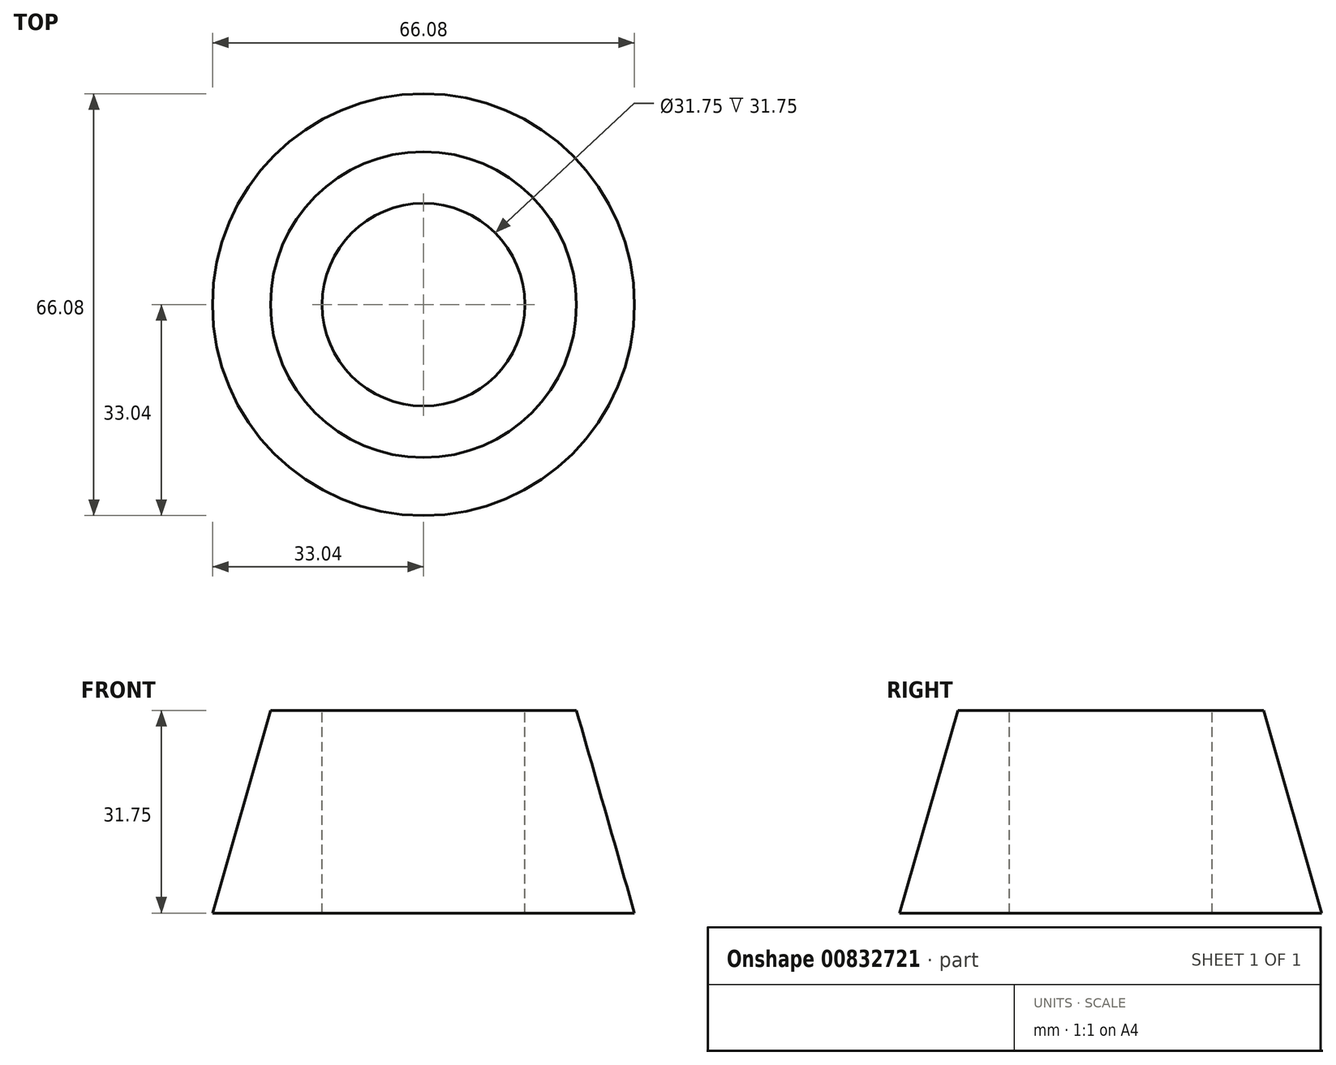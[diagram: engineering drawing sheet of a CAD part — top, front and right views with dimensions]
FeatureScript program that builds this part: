
annotation { "Feature Type Name" : "Feature", "Feature Type Description" : "" }
export const myFeature = defineFeature(function(context is Context, id is Id, definition is map)
    precondition{}
    {
        {
            var Q0;
            Q0=qCreatedBy(makeId("Top.planeOp"),FACE);
            var sketch = newSketch(context, id + "F0", { "sketchPlane" : qUnion([Q0])});
            skCircle(sketch, "E0", {"center": v(0, 0) * mm, "radius": 33.04 * mm});
            skSolve(sketch);
        }
        {
            var Q0;
            Q0=qCreatedBy(makeId("Top.planeOp"),FACE);
            cPlane(context, id + "F1", {"entities" : qUnion([Q0]), "cplaneType" : CPlaneType.OFFSET, "offset" : 31.75 * mm, "width" : 152.4 * mm, "height" : 152.4 * mm});
        }
        {
            var Q0;
            Q0=qCreatedBy(id+"F1.planeOp",FACE);
            var sketch = newSketch(context, id + "F2", { "sketchPlane" : qUnion([Q0])});
            skCircle(sketch, "E1", {"center": v(0, 0) * mm, "radius": 23.95 * mm});
            skSolve(sketch);
        }
        {
            var Q0;
            Q0=makeQuery(id+"F0.imprint","IMPRINT",FACE,{"disambiguationData":[TD([[makeQuery(id+"F0.imprint","IMPRINT",EDGE,{"derivedFrom":sQuery(id+"F0.wireOp",EDGE,"E0")}),1.0]])]});
            var Q1;
            Q1=makeQuery(id+"F2.imprint","IMPRINT",FACE,{"disambiguationData":[TD([[makeQuery(id+"F2.imprint","IMPRINT",EDGE,{"derivedFrom":sQuery(id+"F2.wireOp",EDGE,"E1")}),1.0]])]});
            loft(context, id + "F3", {"sheetProfilesArray" : [{ "sheetProfileEntities" : qUnion([Q0]) }, { "sheetProfileEntities" : qUnion([Q1]) }]});
        }
        {
            var Q0;
            Q0=qCreatedBy(id+"F1.planeOp",FACE);
            var sketch = newSketch(context, id + "F4", { "sketchPlane" : qUnion([Q0])});
            skCircle(sketch, "E2", {"center": v(0, 0) * mm, "radius": 13.44 * mm});
            skSolve(sketch);
        }
        {
            var Q0;
            Q0=sQuery(id+"F4.wireOp",VERTEX,"E2.center");
            var Q1;
            Q1=makeQuery(id+"F3.opLoft","SWEPT_BODY",BODY,{"disambiguationData":[OSD([makeQuery(id+"F0.imprint","IMPRINT",FACE,{"disambiguationData":[TD([[makeQuery(id+"F0.imprint","IMPRINT",EDGE,{"derivedFrom":sQuery(id+"F0.wireOp",EDGE,"E0")}),1.0]])]}),makeQuery(id+"F2.imprint","IMPRINT",FACE,{"disambiguationData":[TD([[makeQuery(id+"F2.imprint","IMPRINT",EDGE,{"derivedFrom":sQuery(id+"F2.wireOp",EDGE,"E1")}),1.0]])]})])]});
            hole(context, id + "F5", {"style" : HoleStyle.SIMPLE, "endStyle" : HoleEndStyle.THROUGH, "holeDiameter" : 31.75 * mm, "majorDiameter" : 6.35 * mm, "isTappedThrough" : true, "tappedDepth" : 12.7 * mm, "tapClearance" : 3, "locations" : qUnion([Q0]), "scope" : qUnion([Q1])});
        }
    });
